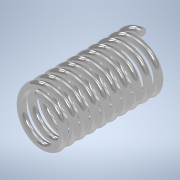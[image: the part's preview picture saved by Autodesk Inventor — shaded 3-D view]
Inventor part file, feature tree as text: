
AUTODESK INVENTOR PART (.ipt)
format: ipt  version: 2022 (Build 260153000, 153)  size: 404,480 bytes
history: native  units: mm
features: sketch x2, other x1, extrude x1
ambient origin geometry x8: Origin, YZ Plane, XZ Plane, XY Plane, X Axis, Y Axis, Z Axis, Center Point
bodies: Volumenkörper1 (feature_tree)
feature tree (4):
  other  "Spirale1"
  extrude  "Extrusion1"  Depth=1.0mm TaperAngle=0.0deg
  sketch  "Skizze1"  dims[d0=1.0mm]
  sketch  "Skizze2"  dims[d1=1.5mm d2=10.0mm d3=100.0mm d4=0.0mm d5=90.0deg d6=90.0deg d7=0.0mm d8=0.0mm d9=1.0mm d10=0.0mm]
